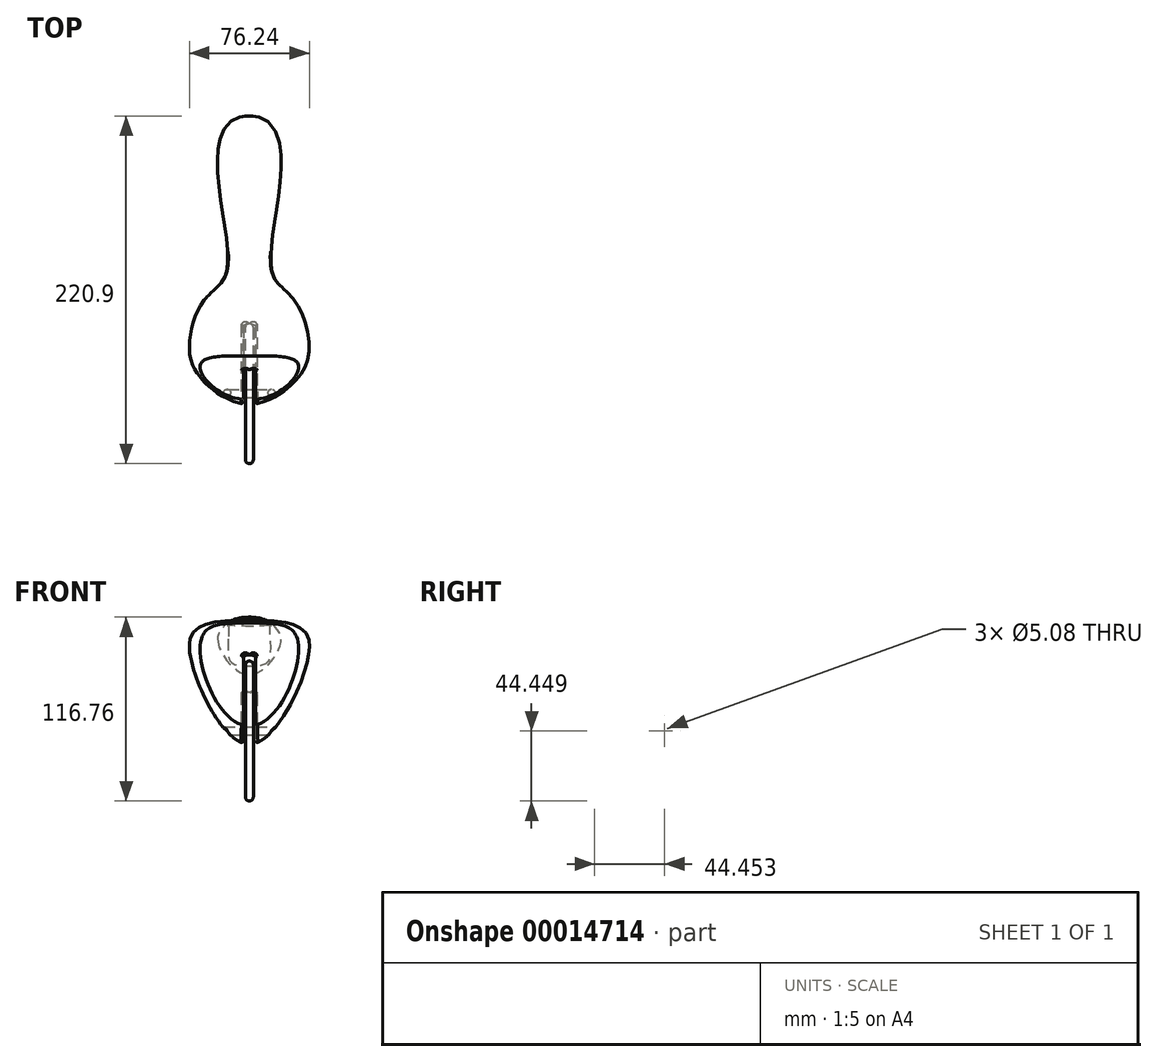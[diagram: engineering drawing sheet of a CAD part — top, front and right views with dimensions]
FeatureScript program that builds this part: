
annotation { "Feature Type Name" : "Feature", "Feature Type Description" : "" }
export const myFeature = defineFeature(function(context is Context, id is Id, definition is map)
    precondition{}
    {
        {
            var Q0;
            Q0=qCreatedBy(makeId("Top.planeOp"),FACE);
            cPlane(context, id + "F0", {"entities" : qUnion([Q0]), "cplaneType" : CPlaneType.OFFSET, "offset" : 12.7 * mm, "width" : 152.4 * mm, "height" : 152.4 * mm});
        }
        {
            var Q0;
            Q0=qCreatedBy(makeId("Right.planeOp"),FACE);
            var sketch = newSketch(context, id + "F1", { "sketchPlane" : qUnion([Q0])});
            skFitSpline(sketch, "E0", {"points": [v(0, 22.63) * mm, v(31.69, 21) * mm, v(103.66, 26.37) * mm, v(152.4, 12.7) * mm], "startDerivative": vector(24.11, 56.35) * mm, "endDerivative": vector(0, -91.8) * mm});
            skFitSpline(sketch, "E1", {"points": [v(152.4, 12.7) * mm, v(123.34, -10.02) * mm, v(34.56, -13.34) * mm, v(-27.97, -42.75) * mm], "startDerivative": vector(0, -121.83) * mm, "endDerivative": vector(121.15, 283.17) * mm});
            skCircle(sketch, "E2", {"center": v(-24.05, -45.9) * mm, "radius": 50.8 * mm, "construction": true});
            skLineSegment(sketch, "E3", {"start": v(0, 22.63) * mm, "end": v(-27.97, -42.75) * mm});
            skSolve(sketch);
        }
        {
            var Q0;
            Q0=qCreatedBy(id+"F0.planeOp",FACE);
            var sketch = newSketch(context, id + "F2", { "sketchPlane" : qUnion([Q0])});
            skLineSegment(sketch, "E4", {"start": v(30.48, -4.25) * mm, "end": v(0, -4.25) * mm});
            skLineSegment(sketch, "E5", {"start": v(0, -4.25) * mm, "end": v(0, 152.4) * mm, "construction": true});
            skFitSpline(sketch, "E6", {"points": [v(30.48, -4.25) * mm, v(31.84, 30.36) * mm, v(14.9, 51.38) * mm, v(19.5, 109.76) * mm, v(0, 152.4) * mm], "startDerivative": vector(142.97, 0) * mm, "endDerivative": vector(-227.78, 0) * mm});
            skLineSegment(sketch, "E7.MirrorCS", {"start": v(-30.48, -4.25) * mm, "end": v(0, -4.25) * mm});
            skFitSpline(sketch, "E8.MirrorCS", {"points": [v(-30.48, -4.25) * mm, v(-31.84, 30.36) * mm, v(-14.9, 51.38) * mm, v(-19.5, 109.76) * mm, v(0, 152.4) * mm], "startDerivative": vector(-142.97, 0) * mm, "endDerivative": vector(227.78, 0) * mm});
            skSolve(sketch);
        }
        {
            var Q0;
            Q0=sQuery(id+"F1.wireOp",VERTEX,"E0.start");
            var Q1;
            Q1=sQuery(id+"F2.wireOp",VERTEX,"E5.start");
            var Q2;
            Q2=sQuery(id+"F2.wireOp",VERTEX,"E6.start");
            cPlane(context, id + "F3", {"entities" : qUnion([Q0, Q1, Q2]), "cplaneType" : CPlaneType.THREE_POINT, "offset" : 152.4 * mm, "width" : 152.4 * mm, "height" : 152.4 * mm});
        }
        {
            var Q0;
            Q0=qCreatedBy(id+"F3.planeOp",FACE);
            var sketch = newSketch(context, id + "F4", { "sketchPlane" : qUnion([Q0])});
            skLineSegment(sketch, "E9", {"start": v(0, 33.33) * mm, "end": v(0, -50.3) * mm, "construction": true});
            skFitSpline(sketch, "E10", {"points": [v(0, 20.8) * mm, v(30.48, 10) * mm, v(0, -50.3) * mm], "startDerivative": vector(106.7, 0) * mm, "endDerivative": vector(-99.08, 0) * mm});
            skFitSpline(sketch, "E11.MirrorCS", {"points": [v(0, 20.8) * mm, v(-30.48, 10) * mm, v(0, -50.3) * mm], "startDerivative": vector(-106.7, 0) * mm, "endDerivative": vector(99.08, 0) * mm});
            skSolve(sketch);
        }
        {
            var Q0;
            Q0=sQuery(id+"F2.wireOp",VERTEX,"E6.3.internal");
            var Q1;
            Q1=qCreatedBy(makeId("Front.planeOp"),FACE);
            cPlane(context, id + "F5", {"entities" : qUnion([Q0, Q1]), "cplaneType" : CPlaneType.PLANE_POINT, "offset" : 152.4 * mm, "width" : 152.4 * mm, "height" : 152.4 * mm});
        }
        {
            var Q0;
            Q0=qCreatedBy(id+"F5.planeOp",FACE);
            var sketch = newSketch(context, id + "F6", { "sketchPlane" : qUnion([Q0])});
            skFitSpline(sketch, "E12", {"points": [v(0, 26.4) * mm, v(19.5, 12.7) * mm, v(0, -9.75) * mm], "startDerivative": vector(68.63, 0) * mm, "endDerivative": vector(-57.85, 0) * mm});
            skLineSegment(sketch, "E13", {"start": v(0, 26.4) * mm, "end": v(0, 7.7) * mm, "construction": true});
            skFitSpline(sketch, "E14.MirrorCS", {"points": [v(0, 26.4) * mm, v(-19.5, 12.7) * mm, v(0, -9.75) * mm], "startDerivative": vector(-68.63, 0) * mm, "endDerivative": vector(57.85, 0) * mm});
            skSolve(sketch);
        }
        {
            var Q0;
            Q0=makeQuery(id+"F4.imprint","IMPRINT",FACE,{"disambiguationData":[TD([[makeQuery(id+"F4.imprint","IMPRINT",EDGE,{"derivedFrom":sQuery(id+"F4.wireOp",EDGE,"E10")}),-1.0]])]});
            var Q1;
            Q1=makeQuery(id+"F6.imprint","IMPRINT",FACE,{"disambiguationData":[TD([[makeQuery(id+"F6.imprint","IMPRINT",EDGE,{"derivedFrom":sQuery(id+"F6.wireOp",EDGE,"E12")}),-1.0]])]});
            var Q2;
            Q2=sQuery(id+"F2.wireOp",VERTEX,"E6.end");
            var Q3;
            Q3=sQuery(id+"F2.wireOp",EDGE,"E6");
            var Q4;
            Q4=sQuery(id+"F2.wireOp",EDGE,"E8.MirrorCS");
            var Q5;
            Q5=sQuery(id+"F1.wireOp",EDGE,"E1");
            var Q6;
            Q6=sQuery(id+"F1.wireOp",EDGE,"E0");
            loft(context, id + "F7", {"addGuides" : true, "sheetProfilesArray" : [{ "sheetProfileEntities" : qUnion([Q0]) }, { "sheetProfileEntities" : qUnion([Q1]) }, { "sheetProfileEntities" : qUnion([Q2]) }], "guidesArray" : [{ "guideEntities" : qUnion([Q3]), "guideDerivativeType" : LoftGuideDerivativeType.DEFAULT, "guideDerivativeMagnitude" : 1 }, { "guideEntities" : qUnion([Q4]), "guideDerivativeType" : LoftGuideDerivativeType.DEFAULT, "guideDerivativeMagnitude" : 1 }, { "guideEntities" : qUnion([Q5]), "guideDerivativeType" : LoftGuideDerivativeType.DEFAULT, "guideDerivativeMagnitude" : 1 }, { "guideEntities" : qUnion([Q6]), "guideDerivativeType" : LoftGuideDerivativeType.DEFAULT, "guideDerivativeMagnitude" : 1 }]});
        }
        {
            var Q0;
            Q0=qCreatedBy(makeId("Right.planeOp"),FACE);
            var sketch = newSketch(context, id + "F8", { "sketchPlane" : qUnion([Q0])});
            skCircle(sketch, "E15.0", {"center": v(-24.05, -45.9) * mm, "radius": 50.8 * mm});
            skSolve(sketch);
        }
        {
            var Q0;
            Q0=makeQuery(id+"F8.imprint","IMPRINT",FACE,{"disambiguationData":[TD([[makeQuery(id+"F8.imprint","IMPRINT",EDGE,{"derivedFrom":sQuery(id+"F8.wireOp",EDGE,"E15.0")}),1.0]])]});
            extrude(context, id + "F9", {"entities" : qUnion([Q0]), "operationType" : NewBodyOperationType.REMOVE, "endBound" : BoundingType.SYMMETRIC, "oppositeDirection" : true, "depth" : 7.62 * mm});
        }
        {
            var Q0;
            Q0=makeQuery(id+"F9.boolean.opBoolean","COPY",FACE,{"derivedFrom":makeQuery(id+"F9.opExtrude","CAP_FACE",FACE,{"disambiguationData":[OSD([sQuery(id+"F8.wireOp",EDGE,"E15.0")])],"isStart":false})});
            var Q1;
            Q1=makeQuery(id+"F9.boolean.opBoolean","COPY",FACE,{"derivedFrom":makeQuery(id+"F9.opExtrude","CAP_FACE",FACE,{"disambiguationData":[OSD([sQuery(id+"F8.wireOp",EDGE,"E15.0")])],"isStart":true})});
            fillet(context, id + "F10", {"entities" : qUnion([Q0, Q1]), "radius" : 1.27 * mm, "tangentPropagation" : true, "allowEdgeOverflow" : false});
        }
        {
            var Q0;
            Q0=qCreatedBy(makeId("Right.planeOp"),FACE);
            var sketch = newSketch(context, id + "F11", { "sketchPlane" : qUnion([Q0])});
            skCircle(sketch, "E16", {"center": v(-24.05, -45.9) * mm, "radius": 44.45 * mm});
            skSolve(sketch);
        }
        {
            var Q0;
            Q0=makeQuery(id+"F11.imprint","IMPRINT",FACE,{"disambiguationData":[TD([[makeQuery(id+"F11.imprint","IMPRINT",EDGE,{"derivedFrom":sQuery(id+"F11.wireOp",EDGE,"E16")}),1.0]])]});
            extrude(context, id + "F12", {"entities" : qUnion([Q0]), "endBound" : BoundingType.SYMMETRIC, "depth" : 5.08 * mm});
        }
        {
            var Q0;
            Q0=makeQuery(id+"F12.opExtrude","SWEPT_FACE",FACE,{"disambiguationData":[OSD([sQuery(id+"F11.wireOp",EDGE,"E16")])]});
            fillet(context, id + "F13", {"entities" : qUnion([Q0]), "radius" : 2.54 * mm, "tangentPropagation" : true, "allowEdgeOverflow" : false});
        }
        {
            var Q0;
            Q0=qCreatedBy(makeId("Right.planeOp"),FACE);
            var sketch = newSketch(context, id + "F14", { "sketchPlane" : qUnion([Q0])});
            skCircle(sketch, "E17", {"center": v(-24.05, -45.9) * mm, "radius": 2.54 * mm});
            skSolve(sketch);
        }
        {
            var Q0;
            Q0 = qSketchRegion(id + "F14", true);
            extrude(context, id + "F15", {"entities" : qUnion([Q0]), "operationType" : NewBodyOperationType.REMOVE, "endBound" : BoundingType.THROUGH_ALL, "oppositeDirection" : true, "depth" : 25.4 * mm, "hasSecondDirection" : true, "secondDirectionBound" : SecondDirectionBoundingType.THROUGH_ALL, "secondDirectionOppositeDirection" : false, "secondDirectionDepth" : 25.4 * mm});
        }
    });
